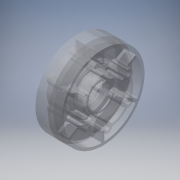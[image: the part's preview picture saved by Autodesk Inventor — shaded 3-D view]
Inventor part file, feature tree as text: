
AUTODESK INVENTOR PART (.ipt)
format: ipt  version: 2016 (Build 200138000, 138)  size: 1,620,480 bytes
history: native  units: in
note: dims shown in document units (in); Inventor stores cm internally (conversion verified against a paired STEP export)
features: fillet x2
ambient origin geometry x8: Origin, YZ Plane, XZ Plane, XY Plane, X Axis, Y Axis, Z Axis, Center Point
bodies: Solid1 (feature_tree), Solid2 (feature_tree)
feature tree (2):
  fillet  "Fillet10"  [1 undecoded]
  fillet  "Fillet9"  [1 undecoded]
note: 2 required parameter values undecoded (feature->parameter linkage not recoverable at this tier; creation-order binding heuristic only, values carry confidence <= 0.55)
